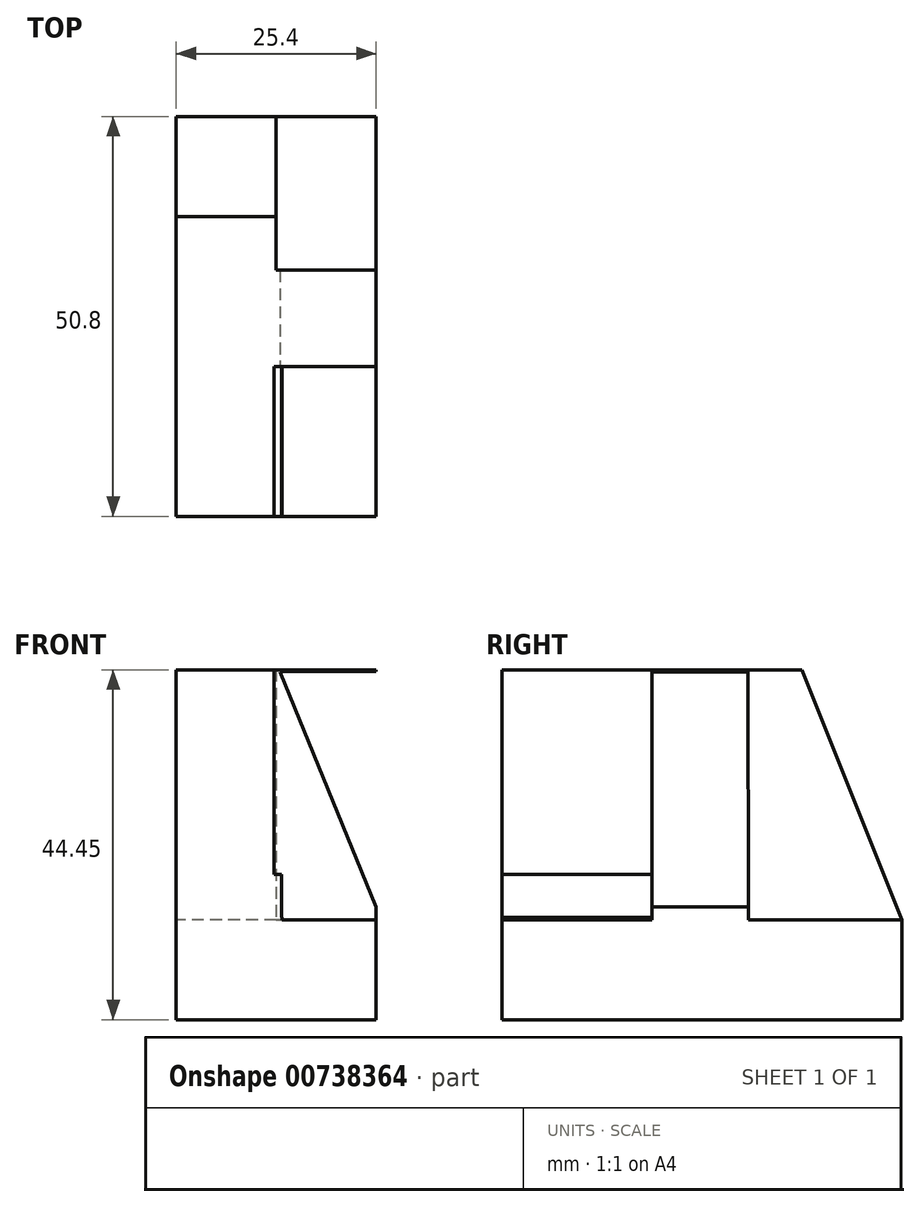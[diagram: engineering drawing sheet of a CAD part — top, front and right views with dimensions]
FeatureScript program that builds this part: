
annotation { "Feature Type Name" : "Feature", "Feature Type Description" : "" }
export const myFeature = defineFeature(function(context is Context, id is Id, definition is map)
    precondition{}
    {
        {
            var Q0;
            Q0=qCreatedBy(makeId("Right.planeOp"),FACE);
            var sketch = newSketch(context, id + "F0", { "sketchPlane" : qUnion([Q0])});
            skLineSegment(sketch, "E0", {"start": v(0, 0) * mm, "end": v(0, 44.45) * mm});
            skLineSegment(sketch, "E1", {"start": v(0, 44.45) * mm, "end": v(38.1, 44.45) * mm});
            skLineSegment(sketch, "E2", {"start": v(38.1, 44.45) * mm, "end": v(50.8, 12.7) * mm});
            skLineSegment(sketch, "E3", {"start": v(50.8, 12.7) * mm, "end": v(50.8, 0) * mm});
            skLineSegment(sketch, "E4", {"start": v(50.8, 0) * mm, "end": v(0, 0) * mm});
            skSolve(sketch);
        }
        {
            var Q0;
            Q0 = qSketchRegion(id + "F0", true);
            extrude(context, id + "F1", {"entities" : qUnion([Q0]), "depth" : 25.4 * mm, "offsetDistance" : 25.4 * mm});
        }
        {
            var Q0;
            Q0=qCreatedBy(makeId("Front.planeOp"),FACE);
            var sketch = newSketch(context, id + "F2", { "sketchPlane" : qUnion([Q0])});
            skLineSegment(sketch, "E5", {"start": v(12.4, 44.56) * mm, "end": v(12.4, 18.48) * mm});
            skLineSegment(sketch, "E6", {"start": v(12.4, 18.48) * mm, "end": v(25.4, 18.48) * mm});
            skLineSegment(sketch, "E7", {"start": v(25.4, 18.48) * mm, "end": v(25.4, 44.4) * mm});
            skLineSegment(sketch, "E8", {"start": v(25.4, 44.4) * mm, "end": v(12.4, 44.56) * mm});
            skSolve(sketch);
        }
        {
            var Q0;
            Q0 = qSketchRegion(id + "F2", true);
            extrude(context, id + "F3", {"entities" : qUnion([Q0]), "operationType" : NewBodyOperationType.REMOVE, "oppositeDirection" : true, "depth" : 19.05 * mm, "offsetDistance" : 25.4 * mm});
        }
        {
            var Q0;
            Q0=qCreatedBy(makeId("Top.planeOp"),FACE);
            var sketch = newSketch(context, id + "F4", { "sketchPlane" : qUnion([Q0])});
            skLineSegment(sketch, "E9", {"start": v(21.4, 19) * mm, "end": v(25.83, 19) * mm});
            skLineSegment(sketch, "E10", {"start": v(25.83, 19) * mm, "end": v(25.83, 0) * mm});
            skLineSegment(sketch, "E11", {"start": v(25.83, 0) * mm, "end": v(21.2, 0) * mm});
            skLineSegment(sketch, "E12", {"start": v(21.2, 0) * mm, "end": v(21.4, 19) * mm});
            skSolve(sketch);
        }
        {
            var Q0;
            Q0 = qSketchRegion(id + "F4", true);
            extrude(context, id + "F5", {"entities" : qUnion([Q0]), "operationType" : NewBodyOperationType.REMOVE, "oppositeDirection" : true, "depth" : 25.4 * mm, "offsetDistance" : 25.4 * mm});
        }
        {
            var Q0;
            Q0=makeQuery(id+"F1.opExtrude","SWEPT_FACE",FACE,{"disambiguationData":[OSD([sQuery(id+"F0.wireOp",EDGE,"E1")])]});
            var sketch = newSketch(context, id + "F6", { "sketchPlane" : qUnion([Q0])});
            skLineSegment(sketch, "E13", {"start": v(21.17, 19.05) * mm, "end": v(25.4, 19.05) * mm});
            skSolve(sketch);
        }
        {
            var Q0;
            Q0 = qSketchRegion(id + "F6", true);
            var Q1;
            {var subQ0=sQuery(id+"F6.wireOp",EDGE,"E13");Q1=makeQuery(id+"F6.imprint","IMPRINT",FACE,{"disambiguationData":[TD([[makeQuery(id+"F6.imprint","IMPRINT",EDGE,{"derivedFrom":subQ0}),-1.0]])]});}
            extrude(context, id + "F7", {"entities" : qUnion([Q0, Q1]), "operationType" : NewBodyOperationType.REMOVE, "oppositeDirection" : true, "depth" : 25.4 * mm, "offsetDistance" : 25.4 * mm});
        }
        {
            var Q0;
            Q0=qCreatedBy(makeId("Front.planeOp"),FACE);
            var sketch = newSketch(context, id + "F8", { "sketchPlane" : qUnion([Q0])});
            skLineSegment(sketch, "E14", {"start": v(13.42, 44.46) * mm, "end": v(13.42, 12.67) * mm});
            skLineSegment(sketch, "E15", {"start": v(13.42, 12.67) * mm, "end": v(25.4, 12.67) * mm});
            skLineSegment(sketch, "E16", {"start": v(25.4, 12.67) * mm, "end": v(25.4, 44.37) * mm});
            skLineSegment(sketch, "E17", {"start": v(25.4, 44.37) * mm, "end": v(13.42, 44.46) * mm});
            skSolve(sketch);
        }
        {
            var Q0;
            Q0 = qSketchRegion(id + "F8", true);
            extrude(context, id + "F9", {"entities" : qUnion([Q0]), "operationType" : NewBodyOperationType.REMOVE, "oppositeDirection" : true, "depth" : 19.05 * mm, "offsetDistance" : 25.4 * mm});
        }
        {
            var Q0;
            Q0=qCreatedBy(makeId("Front.planeOp"),FACE);
            var sketch = newSketch(context, id + "F10", { "sketchPlane" : qUnion([Q0])});
            skLineSegment(sketch, "E18", {"start": v(13.37, 44.73) * mm, "end": v(13.37, 12.97) * mm});
            skLineSegment(sketch, "E19", {"start": v(13.37, 12.97) * mm, "end": v(25.23, 12.97) * mm});
            skLineSegment(sketch, "E20", {"start": v(25.23, 12.97) * mm, "end": v(25.23, 44.53) * mm});
            skLineSegment(sketch, "E21", {"start": v(25.23, 44.53) * mm, "end": v(13.37, 44.73) * mm});
            skSolve(sketch);
        }
        {
            var Q0;
            Q0 = qSketchRegion(id + "F10", true);
            extrude(context, id + "F11", {"entities" : qUnion([Q0]), "operationType" : NewBodyOperationType.REMOVE, "oppositeDirection" : true, "depth" : 19.05 * mm, "offsetDistance" : 25.4 * mm});
        }
        {
            var Q0;
            Q0=makeQuery(id+"F1.opExtrude","CAP_FACE",FACE,{"disambiguationData":[OSD([sQuery(id+"F0.wireOp",EDGE,"E0"),sQuery(id+"F0.wireOp",EDGE,"E1"),sQuery(id+"F0.wireOp",EDGE,"E2"),sQuery(id+"F0.wireOp",EDGE,"E3"),sQuery(id+"F0.wireOp",EDGE,"E4")])],"isStart":false});
            var sketch = newSketch(context, id + "F12", { "sketchPlane" : qUnion([Q0])});
            skLineSegment(sketch, "E22", {"start": v(19.05, 12.67) * mm, "end": v(50.8, 12.7) * mm});
            skLineSegment(sketch, "E23", {"start": v(38.1, 44.45) * mm, "end": v(50.8, 12.7) * mm});
            skLineSegment(sketch, "E24", {"start": v(38.1, 44.45) * mm, "end": v(31.25, 44.45) * mm});
            skLineSegment(sketch, "E25", {"start": v(31.25, 44.45) * mm, "end": v(31.29, 12.67) * mm});
            skSolve(sketch);
        }
        {
            var Q0;
            {var subQ0=sQuery(id+"F12.wireOp",EDGE,"E23");Q0=makeQuery(id+"F12.imprint","IMPRINT",FACE,{"disambiguationData":[TD([[makeQuery(id+"F12.imprint","IMPRINT",EDGE,{"derivedFrom":subQ0}),-1.0]])]});}
            extrude(context, id + "F13", {"entities" : qUnion([Q0]), "operationType" : NewBodyOperationType.REMOVE, "oppositeDirection" : true, "depth" : 12.7 * mm, "offsetDistance" : 25.4 * mm});
        }
        {
            var Q0;
            Q0=qCreatedBy(makeId("Front.planeOp"),FACE);
            var sketch = newSketch(context, id + "F14", { "sketchPlane" : qUnion([Q0])});
            skLineSegment(sketch, "E26", {"start": v(13.2, 44.17) * mm, "end": v(25.75, 13.48) * mm});
            skLineSegment(sketch, "E27", {"start": v(25.75, 13.48) * mm, "end": v(25.75, 44.23) * mm});
            skLineSegment(sketch, "E28", {"start": v(25.75, 44.23) * mm, "end": v(13.2, 44.17) * mm});
            skSolve(sketch);
        }
        {
            var Q0;
            Q0 = qSketchRegion(id + "F14", true);
            extrude(context, id + "F15", {"entities" : qUnion([Q0]), "operationType" : NewBodyOperationType.REMOVE, "endBound" : BoundingType.THROUGH_ALL, "oppositeDirection" : true, "depth" : 25.4 * mm, "offsetDistance" : 25.4 * mm});
        }
    });
